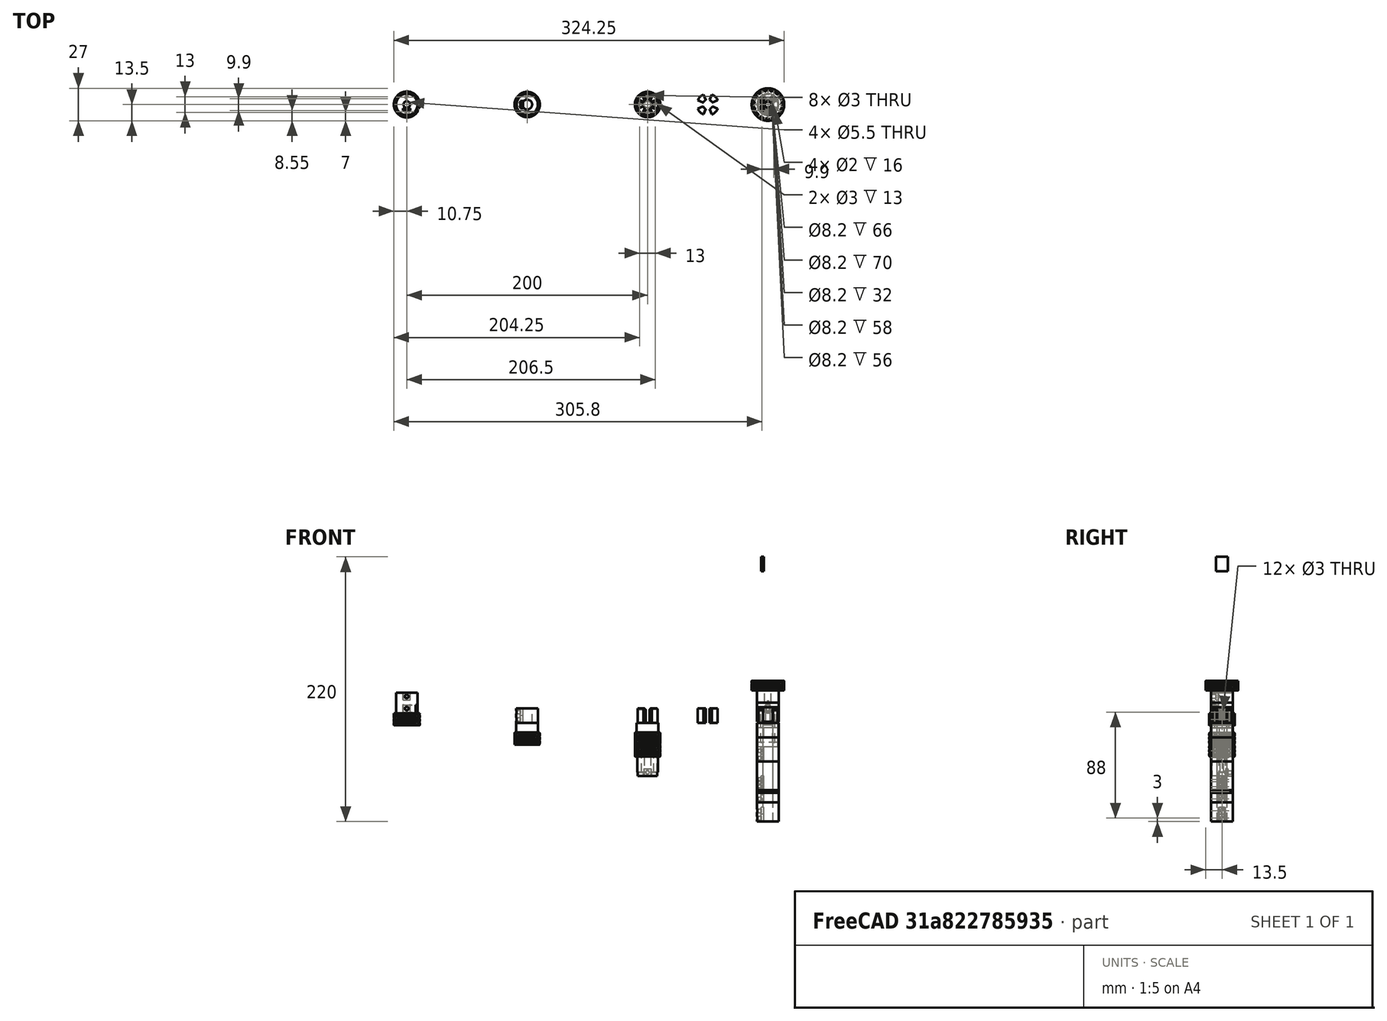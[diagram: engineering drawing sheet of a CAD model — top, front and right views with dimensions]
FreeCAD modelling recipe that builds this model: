
FCSTD DOCUMENT  (FreeCAD 0.19R24276 (Git))
Label: J-max_moto-shaft_009
License: All rights reserved
LicenseURL: http://en.wikipedia.org/wiki/All_rights_reserved
objects: Part::Cylinder×62, Part::Compound×46, Part::Chamfer×44, Part::Cut×37, Part::Wedge×36, Part::FeaturePython×28, Part::Box×18, Part::MultiFuse×3, Mesh::Feature×1
note: 274 computed .brp shape members not serialized (recipe doc carries the construction recipe); baked Part::Feature solids carry a one-line shape summary decoded from their .brp

FEATURE [Part::Cylinder] Cylinder032  label="Válec032"
  Angle = 360
  AttacherType = Attacher::AttachEngine3D
  Height = 3
  Placement = pos=(0,-6,0) rot=(0,0,1;0rad)
  Radius = 3
FEATURE [Part::Cylinder] Cylinder031  label="Válec031"
  Angle = 360
  AttacherType = Attacher::AttachEngine3D
  Height = 17
  Placement = pos=(0,6,3) rot=(0,0,1;0rad)
  Radius = 1.5
FEATURE [Part::Cylinder] Cylinder033  label="Válec033"
  Angle = 360
  AttacherType = Attacher::AttachEngine3D
  Height = 3
  Placement = pos=(0,6,0) rot=(0,0,1;0rad)
  Radius = 3
FEATURE [Part::Cylinder] Cylinder037  label="Válec037"
  Angle = 360
  AttacherType = Attacher::AttachEngine3D
  Height = 100
  Placement = pos=(100,-1,24) rot=(1,0,0;1.5708rad)
  Radius = 1.5
FEATURE [Part::FeaturePython] wormgear006  # WARN: FeaturePython — macro-defined, semantics opaque (R4)
  AttacherType = Attacher::AttachEngine3D
  Placement = pos=(0,0,0) rot=(0,0,1;0.663225rad)
  beta = 31.6075
  clearance = 0.2
  diameter = 19.5
  head = 0
  height = 10
  module = 1
  pressure_angle = 25
  reverse_pitch = true
  teeth = 12
  version = 0.0.3
FEATURE [Part::FeaturePython] wormgear004  # WARN: FeaturePython — macro-defined, semantics opaque (R4)
  AttacherType = Attacher::AttachEngine3D
  Placement = pos=(0,0,10) rot=(0,0,1;0.558505rad)
  beta = 31.6075
  clearance = 0.2
  diameter = 19.5
  head = 0
  height = 10
  module = 1
  pressure_angle = 25
  reverse_pitch = false
  teeth = 12
  version = 0.0.3
FEATURE [Part::Compound] Compound
  Links = -> [wormgear006,wormgear004]
FEATURE [Part::FeaturePython] Compound_child1  label="Compound.1"  # WARN: FeaturePython — macro-defined, semantics opaque (R4)
  Base = -> Compound
  FilterType = 1
  Invert = false
  OverrideMaxVal = 0
  WindowFrom = 80
  WindowTo = 100
  items = 1
FEATURE [Part::FeaturePython] Tube  # WARN: FeaturePython — macro-defined, semantics opaque (R4)
  AttacherType = Attacher::AttachEngine3D
  Height = 17
  InnerRadius = 2.75
  OuterRadius = 9
  Placement = pos=(0,0,20) rot=(0,0,1;0rad)
FEATURE [Part::Cylinder] Cylinder  label="Válec"
  Angle = 360
  AttacherType = Attacher::AttachEngine3D
  Height = 100
  Placement = pos=(100,-1,34) rot=(1,0,0;1.5708rad)
  Radius = 1.5
FEATURE [Part::Cylinder] Cylinder036  label="Válec036"
  Angle = 360
  AttacherType = Attacher::AttachEngine3D
  Height = 17
  Placement = pos=(0,-6,3) rot=(0,0,1;0rad)
  Radius = 1.5
FEATURE [Part::Compound] Compound006
  Links = -> [Cylinder036,Cylinder032,Cylinder033,Cylinder031]
FEATURE [Part::Box] Box  label="Krychle"
  AttacherType = Attacher::AttachEngine3D
  Height = 6
  Length = 6
  Placement = pos=(97,-5,31) rot=(0,0,1;0rad)
  Width = 2
FEATURE [Part::Cylinder] Cylinder019  label="Válec019"
  Angle = 360
  AttacherType = Attacher::AttachEngine3D
  Height = 60
  Placement = pos=(0,0,-10) rot=(0,0,1;0rad)
  Radius = 2.75
FEATURE [Part::Cut] Cut003
  Base = -> Compound_child1
  Tool = -> Cylinder019
FEATURE [Part::Compound] Compound016
  Links = -> [Cut003,Tube]
FEATURE [Part::Cut] Cut014  label="inner_p2"
  Base = -> Compound016
  Placement = pos=(100,0,0) rot=(0,0,1;0rad)
  Tool = -> Compound006
FEATURE [Part::Cut] Cut
  Base = -> Cut014
  Tool = -> Cylinder
FEATURE [Part::Cut] Cut015
  Base = -> Cut
  Tool = -> Box
FEATURE [Part::Box] Box001  label="Krychle001"
  AttacherType = Attacher::AttachEngine3D
  Height = 6
  Length = 14
  Placement = pos=(97,-5,21) rot=(0,0,1;0rad)
  Width = 2
FEATURE [Part::Cut] Cut016
  Base = -> Cut015
  Tool = -> Box001
FEATURE [Part::Cut] Cut017  label="planeo_vnitrni_hladko"
  Base = -> Cut016
  Tool = -> Cylinder037
FEATURE [Part::FeaturePython] Tube001  # WARN: FeaturePython — macro-defined, semantics opaque (R4)
  AttacherType = Attacher::AttachEngine3D
  Height = 12
  InnerRadius = 4.1
  OuterRadius = 9
  Placement = pos=(200,0,12) rot=(0,0,1;0rad)
FEATURE [Part::Box] Box002  label="Krychle002"
  AttacherType = Attacher::AttachEngine3D
  Height = 12
  Length = 2
  Placement = pos=(194.5,-5,12) rot=(0,0,1;0rad)
  Width = 10
FEATURE [Part::Cylinder] Cylinder039  label="Válec039"
  Angle = 360
  AttacherType = Attacher::AttachEngine3D
  Height = 100
  Placement = pos=(100,0,21) rot=(0.57735,0.57735,0.57735;2.0944rad)
  Radius = 1.5
FEATURE [Part::Box] Box003  label="Krychle003"
  AttacherType = Attacher::AttachEngine3D
  Height = 6
  Length = 6
  Placement = pos=(196.5,-3,18) rot=(0,0,1;1.5708rad)
  Width = 2
FEATURE [Part::MultiFuse] Fusion
  Shapes = -> [Tube001,Box002]
FEATURE [Part::Box] Box004  label="Krychle004"
  AttacherType = Attacher::AttachEngine3D
  Height = 6
  Length = 6
  Placement = pos=(196.5,-3,12) rot=(0,0,1;1.5708rad)
  Width = 2
FEATURE [Part::Cylinder] Cylinder040  label="Válec040"
  Angle = 360
  AttacherType = Attacher::AttachEngine3D
  Height = 100
  Placement = pos=(100,0,15) rot=(0.57735,0.57735,0.57735;2.0944rad)
  Radius = 1.5
FEATURE [Part::Compound] Compound017
  Links = -> [Box003,Box004]
FEATURE [Part::Cut] Cut018
  Base = -> Fusion
  Tool = -> Compound017
FEATURE [Part::Cylinder] Cylinder041  label="Válec041"
  Angle = 360
  AttacherType = Attacher::AttachEngine3D
  Height = 8
  Placement = pos=(200,0,4) rot=(0,0,1;0rad)
  Radius = 9
FEATURE [Part::Cylinder] Cylinder042  label="Válec042"
  Angle = 360
  AttacherType = Attacher::AttachEngine3D
  Height = 3
  Placement = pos=(0,-6.5,0) rot=(0,0,1;0rad)
  Radius = 3
FEATURE [Part::Cylinder] Cylinder043  label="Válec043"
  Angle = 360
  AttacherType = Attacher::AttachEngine3D
  Height = 3
  Placement = pos=(0,6.5,0) rot=(0,0,1;0rad)
  Radius = 3
FEATURE [Part::Cylinder] Cylinder044  label="Válec044"
  Angle = 360
  AttacherType = Attacher::AttachEngine3D
  Height = 26
  Placement = pos=(0,-6.5,3) rot=(0,0,1;0rad)
  Radius = 1.5
FEATURE [Part::Cylinder] Cylinder045  label="Válec045"
  Angle = 360
  AttacherType = Attacher::AttachEngine3D
  Height = 26
  Placement = pos=(0,6.5,3) rot=(0,0,1;0rad)
  Radius = 1.5
FEATURE [Part::Compound] Compound019
  Links = -> [Cylinder044,Cylinder042,Cylinder043,Cylinder045]
  Placement = pos=(200,0,-25) rot=(0,0,1;0rad)
FEATURE [Part::FeaturePython] wormgear007  # WARN: FeaturePython — macro-defined, semantics opaque (R4)
  AttacherType = Attacher::AttachEngine3D
  Placement = pos=(200,0,-6) rot=(0,0,1;0.558505rad)
  beta = 32.2756
  clearance = 0.2
  diameter = 19
  head = 0
  height = 10
  module = 1
  pressure_angle = 25
  reverse_pitch = true
  teeth = 12
  version = 0.0.3
FEATURE [Part::Cut] Cut020
  Base = -> wormgear007
  Tool = -> Compound019
FEATURE [Part::Compound] Compound018
  Links = -> [Cylinder039,Cylinder040]
FEATURE [Part::Cut] Cut019  label="super_spojka"
  Base = -> Cut018
  Tool = -> Compound018
FEATURE [Part::Compound] Compound020  label="super_spojka_s_vnitrnim_koleckem"
  Links = -> [Cylinder041,Cut020,Cut019]
FEATURE [Part::FeaturePython] Tube002  # WARN: FeaturePython — macro-defined, semantics opaque (R4)
  AttacherType = Attacher::AttachEngine3D
  Height = 12
  InnerRadius = 4.1
  OuterRadius = 9
  Placement = pos=(300,0,12) rot=(0,0,1;0rad)
FEATURE [Part::Cylinder] Cylinder046  label="Válec046"
  Angle = 360
  AttacherType = Attacher::AttachEngine3D
  Height = 8
  Placement = pos=(300,0,4) rot=(0,0,1;0rad)
  Radius = 9
FEATURE [Part::Cylinder] Cylinder047  label="Válec047"
  Angle = 360
  AttacherType = Attacher::AttachEngine3D
  Height = 26
  Placement = pos=(0,6.5,3) rot=(0,0,1;0rad)
  Radius = 1.5
FEATURE [Part::FeaturePython] wormgear008  # WARN: FeaturePython — macro-defined, semantics opaque (R4)
  AttacherType = Attacher::AttachEngine3D
  Placement = pos=(200,0,-6) rot=(0,0,1;0.558505rad)
  beta = 32.14
  clearance = 0.2
  diameter = 19.1
  head = 0
  height = 10
  module = 1
  pressure_angle = 25
  reverse_pitch = true
  teeth = 12
  version = 0.0.3
FEATURE [Part::Cylinder] Cylinder048  label="Válec048"
  Angle = 360
  AttacherType = Attacher::AttachEngine3D
  Height = 26
  Placement = pos=(0,-6.5,3) rot=(0,0,1;0rad)
  Radius = 1.5
FEATURE [Part::Cylinder] Cylinder049  label="Válec049"
  Angle = 360
  AttacherType = Attacher::AttachEngine3D
  Height = 3
  Placement = pos=(0,-6.5,0) rot=(0,0,1;0rad)
  Radius = 3
FEATURE [Part::Cylinder] Cylinder050  label="Válec050"
  Angle = 360
  AttacherType = Attacher::AttachEngine3D
  Height = 3
  Placement = pos=(0,6.5,0) rot=(0,0,1;0rad)
  Radius = 3
FEATURE [Part::Compound] Compound021
  Links = -> [Cylinder048,Cylinder049,Cylinder050,Cylinder047]
  Placement = pos=(200,0,-25) rot=(0,0,1;0rad)
FEATURE [Part::Cut] Cut021
  Base = -> wormgear008
  Placement = pos=(100,0,0) rot=(0,0,1;0rad)
  Tool = -> Compound021
FEATURE [Part::Wedge] Wedge  label="Klín"
  AttacherType = Attacher::AttachEngine3D
  Placement = pos=(300,0,12) rot=(0,0,1;0rad)
  X2max = 0
  X2min = 0
  Xmax = 10
  Xmin = -10
  Ymax = 0
  Ymin = -24.14
  Z2max = 12
  Z2min = 0
  Zmax = 12
  Zmin = 0
FEATURE [Part::Wedge] Wedge001  label="Klín001"
  AttacherType = Attacher::AttachEngine3D
  Placement = pos=(300,0,12) rot=(0,0,1;1.5708rad)
  X2max = 0
  X2min = 0
  Xmax = 10
  Xmin = -10
  Ymax = 0
  Ymin = -24.14
  Z2max = 12
  Z2min = 0
  Zmax = 12
  Zmin = 0
FEATURE [Part::Wedge] Wedge002  label="Klín002"
  AttacherType = Attacher::AttachEngine3D
  Placement = pos=(300,0,12) rot=(0,0,1;3.14159rad)
  X2max = 0
  X2min = 0
  Xmax = 10
  Xmin = -10
  Ymax = 0
  Ymin = -24.14
  Z2max = 12
  Z2min = 0
  Zmax = 12
  Zmin = 0
FEATURE [Part::Wedge] Wedge003  label="Klín003"
  AttacherType = Attacher::AttachEngine3D
  Placement = pos=(300,0,12) rot=(0,0,-1;1.5708rad)
  X2max = 0
  X2min = 0
  Xmax = 10
  Xmin = -10
  Ymax = 0
  Ymin = -24.14
  Z2max = 12
  Z2min = 0
  Zmax = 12
  Zmin = 0
FEATURE [Part::Compound] Compound022
  Links = -> [Wedge,Wedge001,Wedge002,Wedge003]
FEATURE [Part::Cut] Cut022
  Base = -> Tube002
  Tool = -> Compound022
FEATURE [Part::FeaturePython] Tube003  # WARN: FeaturePython — macro-defined, semantics opaque (R4)
  AttacherType = Attacher::AttachEngine3D
  Height = 12
  InnerRadius = 4.1
  OuterRadius = 9
  Placement = pos=(300,0,12) rot=(0,0,1;0rad)
FEATURE [Part::Wedge] Wedge004  label="Klín004"
  AttacherType = Attacher::AttachEngine3D
  Placement = pos=(300,0,12) rot=(0,0,1;1.5708rad)
  X2max = 0
  X2min = 0
  Xmax = 10
  Xmin = -10
  Ymax = 0
  Ymin = -24.14
  Z2max = 12
  Z2min = 0
  Zmax = 12
  Zmin = 0
FEATURE [Part::Wedge] Wedge005  label="Klín005"
  AttacherType = Attacher::AttachEngine3D
  Placement = pos=(300,0,12) rot=(0,0,1;3.14159rad)
  X2max = 0
  X2min = 0
  Xmax = 10
  Xmin = -10
  Ymax = 0
  Ymin = -24.14
  Z2max = 12
  Z2min = 0
  Zmax = 12
  Zmin = 0
FEATURE [Part::Wedge] Wedge006  label="Klín006"
  AttacherType = Attacher::AttachEngine3D
  Placement = pos=(300,0,12) rot=(0,0,-1;1.5708rad)
  X2max = 0
  X2min = 0
  Xmax = 10
  Xmin = -10
  Ymax = 0
  Ymin = -24.14
  Z2max = 12
  Z2min = 0
  Zmax = 12
  Zmin = 0
FEATURE [Part::Wedge] Wedge007  label="Klín007"
  AttacherType = Attacher::AttachEngine3D
  Placement = pos=(300,0,12) rot=(0,0,1;0rad)
  X2max = 0
  X2min = 0
  Xmax = 10
  Xmin = -10
  Ymax = 0
  Ymin = -24.14
  Z2max = 12
  Z2min = 0
  Zmax = 12
  Zmin = 0
FEATURE [Part::Compound] Compound023
  Links = -> [Wedge007,Wedge004,Wedge005,Wedge006]
FEATURE [Part::Cut] Cut023
  Base = -> Tube003
  Placement = pos=(50,0,0) rot=(0,0,1;0rad)
  Tool = -> Compound023
FEATURE [Part::Compound] Compound024
  Links = -> [Cylinder046,Cut021,Cut022]
FEATURE [Part::Chamfer] Chamfer
  Base = -> Compound024
  Edges = 1 edges r=1: [Edge196]
FEATURE [Part::Chamfer] Chamfer001
  Base = -> Chamfer
  Edges = 1 edges r=1: [Edge187]
FEATURE [Part::Chamfer] Chamfer002
  Base = -> Chamfer001
  Edges = 1 edges r=1: [Edge7]
FEATURE [Part::Chamfer] Chamfer003
  Base = -> Chamfer002
  Edges = 1 edges r=1: [Edge196]
FEATURE [Part::Chamfer] Chamfer004
  Base = -> Chamfer003
  Edges = 1 edges r=1: [Edge206]
FEATURE [Part::Chamfer] Chamfer005
  Base = -> Chamfer004
  Edges = 1 edges r=1: [Edge28]
FEATURE [Part::Chamfer] Chamfer006  label="spojka_aktuarni"
  Base = -> Chamfer005
  Edges = 1 edges r=1: [Edge58]
FEATURE [Part::Wedge] Wedge008  label="Klín008"
  AttacherType = Attacher::AttachEngine3D
  Placement = pos=(400,0,12) rot=(0,0,1;0rad)
  X2max = 0
  X2min = 0
  Xmax = 10
  Xmin = -10
  Ymax = 0
  Ymin = -20
  Z2max = 12
  Z2min = 0
  Zmax = 12
  Zmin = 0
FEATURE [Part::Wedge] Wedge009  label="Klín009"
  AttacherType = Attacher::AttachEngine3D
  Placement = pos=(400,0,12) rot=(0,0,1;1.5708rad)
  X2max = 0
  X2min = 0
  Xmax = 10
  Xmin = -10
  Ymax = 0
  Ymin = -20
  Z2max = 12
  Z2min = 0
  Zmax = 12
  Zmin = 0
FEATURE [Part::Wedge] Wedge010  label="Klín010"
  AttacherType = Attacher::AttachEngine3D
  Placement = pos=(400,0,12) rot=(0,0,1;3.14159rad)
  X2max = 0
  X2min = 0
  Xmax = 10
  Xmin = -10
  Ymax = 0
  Ymin = -20
  Z2max = 12
  Z2min = 0
  Zmax = 12
  Zmin = 0
FEATURE [Part::Wedge] Wedge011  label="Klín011"
  AttacherType = Attacher::AttachEngine3D
  Placement = pos=(400,0,12) rot=(0,0,-1;1.5708rad)
  X2max = 0
  X2min = 0
  Xmax = 10
  Xmin = -10
  Ymax = 0
  Ymin = -20
  Z2max = 12
  Z2min = 0
  Zmax = 12
  Zmin = 0
FEATURE [Part::FeaturePython] Tube004  # WARN: FeaturePython — macro-defined, semantics opaque (R4)
  AttacherType = Attacher::AttachEngine3D
  Height = 12
  InnerRadius = 4.1
  OuterRadius = 9
  Placement = pos=(400,0,12) rot=(0,0,1;0rad)
FEATURE [Part::Box] Box005  label="Krychle005"
  AttacherType = Attacher::AttachEngine3D
  Height = 6
  Length = 6
  Placement = pos=(196.5,-3,12) rot=(0,0,1;1.5708rad)
  Width = 2
FEATURE [Part::Cylinder] Cylinder051  label="Válec051"
  Angle = 360
  AttacherType = Attacher::AttachEngine3D
  Height = 100
  Placement = pos=(100,0,15) rot=(0.57735,0.57735,0.57735;2.0944rad)
  Radius = 1.5
FEATURE [Part::Box] Box006  label="Krychle006"
  AttacherType = Attacher::AttachEngine3D
  Height = 12
  Length = 2
  Placement = pos=(194.5,-5,12) rot=(0,0,1;0rad)
  Width = 10
FEATURE [Part::Box] Box007  label="Krychle007"
  AttacherType = Attacher::AttachEngine3D
  Height = 6
  Length = 6
  Placement = pos=(196.5,-3,18) rot=(0,0,1;1.5708rad)
  Width = 2
FEATURE [Part::Compound] Compound025
  Links = -> [Box007,Box005]
  Placement = pos=(0,0,-20) rot=(0,0,1;0rad)
FEATURE [Part::Cylinder] Cylinder052  label="Válec052"
  Angle = 360
  AttacherType = Attacher::AttachEngine3D
  Height = 100
  Placement = pos=(100,0,21) rot=(0.57735,0.57735,0.57735;2.0944rad)
  Radius = 1.5
FEATURE [Part::Compound] Compound026
  Links = -> [Cylinder052,Cylinder051]
  Placement = pos=(0,0,-20) rot=(0,0,1;0rad)
FEATURE [Part::FeaturePython] Tube005  # WARN: FeaturePython — macro-defined, semantics opaque (R4)
  AttacherType = Attacher::AttachEngine3D
  Height = 32
  InnerRadius = 4.1
  OuterRadius = 9
  Placement = pos=(200,0,-8) rot=(0,0,1;0rad)
FEATURE [Part::MultiFuse] Fusion001
  Shapes = -> [Tube005,Box006]
FEATURE [Part::Cut] Cut024
  Base = -> Fusion001
  Tool = -> Compound025
FEATURE [Part::Cut] Cut025  label="super_spojka001"
  Base = -> Cut024
  Placement = pos=(200,0,-12) rot=(0,0,1;0rad)
  Tool = -> Compound026
FEATURE [Part::Compound] Compound027
  Links = -> [Wedge011,Wedge008,Wedge009,Wedge010]
FEATURE [Part::Cut] Cut026
  Base = -> Tube004
  Tool = -> Compound027
FEATURE [Part::Compound] Compound028  label="spojka"
  Links = -> [Cut026,Cut025]
FEATURE [Part::Cylinder] Cylinder053  label="Válec053"
  Angle = 360
  AttacherType = Attacher::AttachEngine3D
  Height = 12
  Placement = pos=(400,0,10) rot=(0,0,1;0rad)
  Radius = 4
FEATURE [Part::Chamfer] Chamfer007
  Base = -> Cylinder053
  Edges = 1 edges r=1: [Edge1]
FEATURE [Part::Chamfer] Chamfer008
  Base = -> Compound028
  Edges = 1 edges r=1: [Edge41]
FEATURE [Part::Chamfer] Chamfer009
  Base = -> Chamfer008
  Edges = 1 edges r=1: [Edge8]
FEATURE [Part::Chamfer] Chamfer010
  Base = -> Chamfer009
  Edges = 1 edges r=1: [Edge52]
FEATURE [Part::Chamfer] Chamfer011
  Base = -> Chamfer010
  Edges = 1 edges r=1: [Edge13]
FEATURE [Part::Chamfer] Chamfer012
  Base = -> Chamfer011
  Edges = 1 edges r=1: [Edge41]
FEATURE [Part::Chamfer] Chamfer013
  Base = -> Chamfer012
  Edges = 1 edges r=1: [Edge56]
FEATURE [Part::Chamfer] Chamfer014
  Base = -> Chamfer013
  Edges = 1 edges r=1: [Edge8]
FEATURE [Part::Chamfer] Chamfer015
  Base = -> Chamfer014
  Edges = 1 edges r=1: [Edge32]
FEATURE [Part::Compound] Compound029  label="spojka_motorova"
  Links = -> [Chamfer015,Chamfer007]
FEATURE [Part::Cylinder] Cylinder054  label="Válec054"
  Angle = 360
  AttacherType = Attacher::AttachEngine3D
  Height = 3
  Placement = pos=(0,-6.5,0) rot=(0,0,1;0rad)
  Radius = 3
FEATURE [Part::Cylinder] Cylinder055  label="Válec055"
  Angle = 360
  AttacherType = Attacher::AttachEngine3D
  Height = 50
  Placement = pos=(0,6.5,3) rot=(0,0,1;0rad)
  Radius = 1.5
FEATURE [Part::Cylinder] Cylinder056  label="Válec056"
  Angle = 360
  AttacherType = Attacher::AttachEngine3D
  Height = 3
  Placement = pos=(0,6.5,0) rot=(0,0,1;0rad)
  Radius = 3
FEATURE [Part::FeaturePython] wormgear009  # WARN: FeaturePython — macro-defined, semantics opaque (R4)
  AttacherType = Attacher::AttachEngine3D
  Placement = pos=(0,0,10) rot=(0,0,1;0.383972rad)
  beta = 32.14
  clearance = 0.2
  diameter = 19.1
  head = 0
  height = 10
  module = 1
  pressure_angle = 25
  reverse_pitch = false
  teeth = 12
  version = 0.0.3
FEATURE [Part::FeaturePython] wormgear010  # WARN: FeaturePython — macro-defined, semantics opaque (R4)
  AttacherType = Attacher::AttachEngine3D
  Placement = pos=(0,0,0) rot=(0,0,1;0.645772rad)
  beta = 30.9638
  clearance = 0.2
  diameter = 20
  head = 0
  height = 10
  module = 1
  pressure_angle = 25
  reverse_pitch = true
  teeth = 12
  version = 0.0.3
FEATURE [Part::Compound] Compound031
  Links = -> [wormgear010,wormgear009]
FEATURE [Part::FeaturePython] Compound_child002  label="Compound.002"  # WARN: FeaturePython — macro-defined, semantics opaque (R4)
  Base = -> Compound031
  FilterType = 1
  Invert = false
  OverrideMaxVal = 0
  WindowFrom = 80
  WindowTo = 100
  items = 1
FEATURE [Part::FeaturePython] Tube006  # WARN: FeaturePython — macro-defined, semantics opaque (R4)
  AttacherType = Attacher::AttachEngine3D
  Height = 16
  InnerRadius = 2.75
  OuterRadius = 8.5
  Placement = pos=(0,0,20) rot=(0,0,1;0rad)
FEATURE [Part::Box] Box008  label="Krychle008"
  AttacherType = Attacher::AttachEngine3D
  Height = 6
  Length = 6
  Placement = pos=(97,-5,30) rot=(0,0,1;0rad)
  Width = 2
FEATURE [Part::Cylinder] Cylinder057  label="Válec057"
  Angle = 360
  AttacherType = Attacher::AttachEngine3D
  Height = 50
  Placement = pos=(0,-6.5,3) rot=(0,0,1;0rad)
  Radius = 1.5
FEATURE [Part::Cylinder] Cylinder058  label="Válec058"
  Angle = 360
  AttacherType = Attacher::AttachEngine3D
  Height = 100
  Placement = pos=(100,-1,33) rot=(1,0,0;1.5708rad)
  Radius = 1.5
FEATURE [Part::Cylinder] Cylinder059  label="Válec059"
  Angle = 360
  AttacherType = Attacher::AttachEngine3D
  Height = 50
  Placement = pos=(0,0,-10) rot=(0,0,1;0rad)
  Radius = 2.75
FEATURE [Part::Cut] Cut027
  Base = -> Compound_child002
  Tool = -> Cylinder059
FEATURE [Part::Compound] Compound030
  Links = -> [Cut027,Tube006]
FEATURE [Part::Compound] Compound032
  Links = -> [Cylinder057,Cylinder054,Cylinder056,Cylinder055]
  Placement = pos=(0,0,36) rot=(0.707107,0.707107,0;3.14159rad)
FEATURE [Part::Cut] Cut029  label="inner_p003"
  Base = -> Compound030
  Placement = pos=(100,0,0) rot=(0,0,1;0rad)
  Tool = -> Compound032
FEATURE [Part::Cut] Cut028
  Base = -> Cut029
  Tool = -> Cylinder058
FEATURE [Part::Cut] Cut030  label="planeo_vnitrni_sroubene"
  Base = -> Cut028
  Placement = pos=(200,0,4) rot=(1,0,0;3.14159rad)
  Tool = -> Box008
FEATURE [Part::Wedge] Wedge012  label="Klín012"
  AttacherType = Attacher::AttachEngine3D
  Placement = pos=(400,0,12) rot=(0,0,1;0rad)
  X2max = 0
  X2min = 0
  Xmax = 10
  Xmin = -10
  Ymax = 0
  Ymin = -20
  Z2max = 12
  Z2min = 0
  Zmax = 12
  Zmin = 0
FEATURE [Part::Wedge] Wedge013  label="Klín013"
  AttacherType = Attacher::AttachEngine3D
  Placement = pos=(400,0,12) rot=(0,0,1;1.5708rad)
  X2max = 0
  X2min = 0
  Xmax = 10
  Xmin = -10
  Ymax = 0
  Ymin = -20
  Z2max = 12
  Z2min = 0
  Zmax = 12
  Zmin = 0
FEATURE [Part::Wedge] Wedge014  label="Klín014"
  AttacherType = Attacher::AttachEngine3D
  Placement = pos=(400,0,12) rot=(0,0,1;3.14159rad)
  X2max = 0
  X2min = 0
  Xmax = 10
  Xmin = -10
  Ymax = 0
  Ymin = -20
  Z2max = 12
  Z2min = 0
  Zmax = 12
  Zmin = 0
FEATURE [Part::Wedge] Wedge015  label="Klín015"
  AttacherType = Attacher::AttachEngine3D
  Placement = pos=(400,0,12) rot=(0,0,-1;1.5708rad)
  X2max = 0
  X2min = 0
  Xmax = 10
  Xmin = -10
  Ymax = 0
  Ymin = -20
  Z2max = 12
  Z2min = 0
  Zmax = 12
  Zmin = 0
FEATURE [Part::Compound] Compound033
  Links = -> [Wedge015,Wedge012,Wedge013,Wedge014]
FEATURE [Part::FeaturePython] Tube007  # WARN: FeaturePython — macro-defined, semantics opaque (R4)
  AttacherType = Attacher::AttachEngine3D
  Height = 12
  InnerRadius = 4.1
  OuterRadius = 8.25
  Placement = pos=(400,0,12) rot=(0,0,1;0rad)
FEATURE [Part::Cut] Cut033
  Base = -> Tube007
  Tool = -> Compound033
FEATURE [Part::Compound] Compound035  label="spojka001"
  Links = -> [Cut033]
FEATURE [Part::Cylinder] Cylinder062  label="Válec062"
  Angle = 360
  AttacherType = Attacher::AttachEngine3D
  Height = 12
  Placement = pos=(400,0,10) rot=(0,0,1;0rad)
  Radius = 4
FEATURE [Part::Chamfer] Chamfer021
  Base = -> Cylinder062
  Edges = 1 edges r=1: [Edge1]
FEATURE [Part::Chamfer] Chamfer022
  Base = -> Compound035
  Edges = 1 edges r=1: [Edge41]
FEATURE [Part::Chamfer] Chamfer023
  Base = -> Chamfer022
  Edges = 1 edges r=1: [Edge8]
FEATURE [Part::Chamfer] Chamfer024
  Base = -> Chamfer023
  Edges = 1 edges r=1: [Edge52]
FEATURE [Part::Chamfer] Chamfer018
  Base = -> Chamfer024
  Edges = 1 edges r=1: [Edge13]
FEATURE [Part::Chamfer] Chamfer016
  Base = -> Chamfer018
  Edges = 1 edges r=1: [Edge41]
FEATURE [Part::Chamfer] Chamfer017
  Base = -> Chamfer016
  Edges = 1 edges r=1: [Edge56]
FEATURE [Part::Chamfer] Chamfer020
  Base = -> Chamfer017
  Edges = 1 edges r=1: [Edge8]
FEATURE [Part::Chamfer] Chamfer019
  Base = -> Chamfer020
  Edges = 1 edges r=1: [Edge32]
FEATURE [Part::Compound] Compound034  label="spojka_motorova_bocni"
  Links = -> [Chamfer019,Chamfer021]
FEATURE [Part::FeaturePython] Tube009  # WARN: FeaturePython — macro-defined, semantics opaque (R4)
  AttacherType = Attacher::AttachEngine3D
  Height = 16
  InnerRadius = 4.1
  OuterRadius = 8.25
  Placement = pos=(400,0,-8) rot=(0,0,1;0rad)
FEATURE [Part::Cylinder] Cylinder063  label="Válec063"
  Angle = 360
  AttacherType = Attacher::AttachEngine3D
  Height = 16
  Placement = pos=(400,0,-4) rot=(0,0,1;0rad)
  Radius = 8.25
FEATURE [Part::Compound] Compound036  label="motorova_spojka_bocni"
  Links = -> [Cylinder063,Compound034]
FEATURE [Part::FeaturePython] Tube010  # WARN: FeaturePython — macro-defined, semantics opaque (R4)
  AttacherType = Attacher::AttachEngine3D
  Height = 12
  InnerRadius = 4.1
  OuterRadius = 9
  Placement = pos=(400,0,12) rot=(0,0,1;0rad)
FEATURE [Part::Cylinder] Cylinder064  label="Válec064"
  Angle = 360
  AttacherType = Attacher::AttachEngine3D
  Height = 100
  Placement = pos=(100,0,15) rot=(0.57735,0.57735,0.57735;2.0944rad)
  Radius = 1.5
FEATURE [Part::Cylinder] Cylinder065  label="Válec065"
  Angle = 360
  AttacherType = Attacher::AttachEngine3D
  Height = 100
  Placement = pos=(100,0,21) rot=(0.57735,0.57735,0.57735;2.0944rad)
  Radius = 1.5
FEATURE [Part::Compound] Compound038
  Links = -> [Cylinder065,Cylinder064]
  Placement = pos=(0,0,-20) rot=(0,0,1;0rad)
FEATURE [Part::Cylinder] Cylinder066  label="Válec066"
  Angle = 360
  AttacherType = Attacher::AttachEngine3D
  Height = 12
  Placement = pos=(400,0,10) rot=(0,0,1;0rad)
  Radius = 4
FEATURE [Part::Box] Box009  label="Krychle009"
  AttacherType = Attacher::AttachEngine3D
  Height = 6
  Length = 6
  Placement = pos=(196.5,-3,12) rot=(0,0,1;1.5708rad)
  Width = 2
FEATURE [Part::Box] Box010  label="Krychle010"
  AttacherType = Attacher::AttachEngine3D
  Height = 6
  Length = 6
  Placement = pos=(196.5,-3,18) rot=(0,0,1;1.5708rad)
  Width = 2
FEATURE [Part::Compound] Compound041
  Links = -> [Box010,Box009]
  Placement = pos=(0,0,-20) rot=(0,0,1;0rad)
FEATURE [Part::Wedge] Wedge016  label="Klín016"
  AttacherType = Attacher::AttachEngine3D
  Placement = pos=(400,0,12) rot=(0,0,1;0rad)
  X2max = 0
  X2min = 0
  Xmax = 10
  Xmin = -10
  Ymax = 0
  Ymin = -19
  Z2max = 12
  Z2min = 0
  Zmax = 12
  Zmin = 0
FEATURE [Part::Wedge] Wedge017  label="Klín017"
  AttacherType = Attacher::AttachEngine3D
  Placement = pos=(400,0,12) rot=(0,0,1;1.5708rad)
  X2max = 0
  X2min = 0
  Xmax = 10
  Xmin = -10
  Ymax = 0
  Ymin = -19
  Z2max = 12
  Z2min = 0
  Zmax = 12
  Zmin = 0
FEATURE [Part::Wedge] Wedge018  label="Klín018"
  AttacherType = Attacher::AttachEngine3D
  Placement = pos=(400,0,12) rot=(0,0,1;3.14159rad)
  X2max = 0
  X2min = 0
  Xmax = 10
  Xmin = -10
  Ymax = 0
  Ymin = -19
  Z2max = 12
  Z2min = 0
  Zmax = 12
  Zmin = 0
FEATURE [Part::Wedge] Wedge019  label="Klín019"
  AttacherType = Attacher::AttachEngine3D
  Placement = pos=(400,0,12) rot=(0,0,-1;1.5708rad)
  X2max = 0
  X2min = 0
  Xmax = 10
  Xmin = -10
  Ymax = 0
  Ymin = -19
  Z2max = 12
  Z2min = 0
  Zmax = 12
  Zmin = 0
FEATURE [Part::Compound] Compound040
  Links = -> [Wedge019,Wedge016,Wedge017,Wedge018]
FEATURE [Part::Cut] Cut034
  Base = -> Tube010
  Tool = -> Compound040
FEATURE [Part::FeaturePython] Tube011  # WARN: FeaturePython — macro-defined, semantics opaque (R4)
  AttacherType = Attacher::AttachEngine3D
  Height = 70
  InnerRadius = 4.1
  OuterRadius = 9
  Placement = pos=(200,0,-8) rot=(0,0,1;0rad)
FEATURE [Part::Chamfer] Chamfer028
  Base = -> Cylinder066
  Edges = 1 edges r=1: [Edge1]
FEATURE [Part::Cylinder] Cylinder185  label="Válec185"
  Angle = 360
  AttacherType = Attacher::AttachEngine3D
  Height = 50
  Placement = pos=(0,0,-10) rot=(0,0,1;0rad)
  Radius = 2.65
FEATURE [Part::FeaturePython] wormgear030  # WARN: FeaturePython — macro-defined, semantics opaque (R4)
  AttacherType = Attacher::AttachEngine3D
  Placement = pos=(0,0,29) rot=(0,0,1;0.994838rad)
  beta = 30.9638
  clearance = 0.25
  diameter = 25
  head = 0
  height = 8
  module = 1
  pressure_angle = 20
  reverse_pitch = false
  teeth = 15
  version = 0.0.3
FEATURE [Part::Cut] Cut081
  Base = -> wormgear030
  Tool = -> Cylinder185
FEATURE [Part::FeaturePython] Tube018  # WARN: FeaturePython — macro-defined, semantics opaque (R4)
  AttacherType = Attacher::AttachEngine3D
  Height = 12
  InnerRadius = 4.1
  OuterRadius = 9
  Placement = pos=(0,0,12) rot=(0,0,1;0rad)
FEATURE [Part::Cylinder] Cylinder186  label="Válec186"
  Angle = 360
  AttacherType = Attacher::AttachEngine3D
  Height = 4
  Placement = pos=(0,0,15) rot=(0,0,1;0rad)
  Radius = 9
FEATURE [Part::Wedge] Wedge020  label="Klín020"
  AttacherType = Attacher::AttachEngine3D
  Placement = pos=(0,0,12) rot=(0,0,1;0rad)
  X2max = 0
  X2min = 0
  Xmax = 10
  Xmin = -10
  Ymax = 0
  Ymin = -32
  Z2max = 12
  Z2min = 0
  Zmax = 12
  Zmin = 0
FEATURE [Part::Wedge] Wedge021  label="Klín021"
  AttacherType = Attacher::AttachEngine3D
  Placement = pos=(0,0,12) rot=(0,0,1;1.5708rad)
  X2max = 0
  X2min = 0
  Xmax = 10
  Xmin = -10
  Ymax = 0
  Ymin = -32
  Z2max = 12
  Z2min = 0
  Zmax = 12
  Zmin = 0
FEATURE [Part::Wedge] Wedge022  label="Klín022"
  AttacherType = Attacher::AttachEngine3D
  Placement = pos=(0,0,12) rot=(0,0,1;3.14159rad)
  X2max = 0
  X2min = 0
  Xmax = 10
  Xmin = -10
  Ymax = 0
  Ymin = -32
  Z2max = 12
  Z2min = 0
  Zmax = 12
  Zmin = 0
FEATURE [Part::Wedge] Wedge023  label="Klín023"
  AttacherType = Attacher::AttachEngine3D
  Placement = pos=(0,0,12) rot=(0,0,-1;1.5708rad)
  X2max = 0
  X2min = 0
  Xmax = 10
  Xmin = -10
  Ymax = 0
  Ymin = -32
  Z2max = 12
  Z2min = 0
  Zmax = 12
  Zmin = 0
FEATURE [Part::Compound] Compound042
  Links = -> [Wedge020,Wedge021,Wedge022,Wedge023]
FEATURE [Part::Cut] Cut082
  Base = -> Tube018
  Placement = pos=(0,0,-9) rot=(0,0,1;0rad)
  Tool = -> Compound042
FEATURE [Part::Chamfer] Chamfer034
  Base = -> Cut082
  Edges = 8 edges r=1: [Edge7,Edge8,Edge21,Edge22,Edge31,Edge32,Edge45,Edge46]
FEATURE [Part::FeaturePython] Tube019  # WARN: FeaturePython — macro-defined, semantics opaque (R4)
  AttacherType = Attacher::AttachEngine3D
  Height = 10
  InnerRadius = 2.65
  OuterRadius = 9
  Placement = pos=(0,0,19) rot=(0,0,1;0rad)
FEATURE [Part::Compound] Compound210  label="J-max_inner-planeo"
  Links = -> [Chamfer034,Tube019,Cylinder186,Cut081]
  Placement = pos=(400,0,10) rot=(0,0,-1;0.785398rad)
FEATURE [Part::Box] Box011  label="Krychle011"
  AttacherType = Attacher::AttachEngine3D
  Height = 12
  Length = 2
  Placement = pos=(194.5,-5,200) rot=(0,0,1;0rad)
  Width = 10
FEATURE [Part::MultiFuse] Fusion002
  Shapes = -> [Tube011,Box011]
FEATURE [Part::Cut] Cut036
  Base = -> Fusion002
  Tool = -> Compound041
FEATURE [Part::Cut] Cut035  label="super_spojka002"
  Base = -> Cut036
  Placement = pos=(200,0,-62) rot=(0,0,1;0rad)
  Tool = -> Compound038
FEATURE [Part::Compound] Compound037  label="spojka002"
  Links = -> [Cut034,Cut035]
FEATURE [Part::Chamfer] Chamfer029
  Base = -> Compound037
  Edges = 1 edges r=1: [Edge41]
FEATURE [Part::Chamfer] Chamfer030
  Base = -> Chamfer029
  Edges = 1 edges r=1: [Edge8]
FEATURE [Part::Chamfer] Chamfer031
  Base = -> Chamfer030
  Edges = 1 edges r=1: [Edge52]
FEATURE [Part::Chamfer] Chamfer032
  Base = -> Chamfer031
  Edges = 1 edges r=1: [Edge13]
FEATURE [Part::Chamfer] Chamfer033
  Base = -> Chamfer032
  Edges = 1 edges r=1: [Edge41]
FEATURE [Part::Chamfer] Chamfer025
  Base = -> Chamfer033
  Edges = 1 edges r=1: [Edge56]
FEATURE [Part::Chamfer] Chamfer026
  Base = -> Chamfer025
  Edges = 1 edges r=1: [Edge8]
FEATURE [Part::Chamfer] Chamfer027
  Base = -> Chamfer026
  Edges = 1 edges r=1: [Edge32]
FEATURE [Part::Compound] Compound039  label="J-max_moto-clutch_old"
  Links = -> [Chamfer027,Chamfer028]
FEATURE [Part::Box] Box012  label="Krychle012"
  AttacherType = Attacher::AttachEngine3D
  Height = 6
  Length = 6
  Placement = pos=(196.5,-3,12) rot=(0,0,1;1.5708rad)
  Width = 2
FEATURE [Part::Box] Box013  label="Krychle013"
  AttacherType = Attacher::AttachEngine3D
  Height = 6
  Length = 6
  Placement = pos=(196.5,-3,18) rot=(0,0,1;1.5708rad)
  Width = 2
FEATURE [Part::Cylinder] Cylinder187  label="Válec187"
  Angle = 360
  AttacherType = Attacher::AttachEngine3D
  Height = 100
  Placement = pos=(100,0,15) rot=(0.57735,0.57735,0.57735;2.0944rad)
  Radius = 1.5
FEATURE [Part::Cylinder] Cylinder188  label="Válec188"
  Angle = 360
  AttacherType = Attacher::AttachEngine3D
  Height = 100
  Placement = pos=(100,0,21) rot=(0.57735,0.57735,0.57735;2.0944rad)
  Radius = 1.5
FEATURE [Part::Compound] Compound211
  Links = -> [Cylinder188,Cylinder187]
  Placement = pos=(0,0,-20) rot=(0,0,1;0rad)
FEATURE [Part::Compound] Compound212
  Links = -> [Box013,Box012]
  Placement = pos=(0,0,-20) rot=(0,0,1;0rad)
FEATURE [Part::FeaturePython] Tube020  # WARN: FeaturePython — macro-defined, semantics opaque (R4)
  AttacherType = Attacher::AttachEngine3D
  Height = 56
  InnerRadius = 4.1
  OuterRadius = 9
  Placement = pos=(200,0,-8) rot=(0,0,1;0rad)
FEATURE [Part::Cut] Cut083
  Base = -> Tube020
  Tool = -> Compound212
FEATURE [Part::Cut] Cut084
  Base = -> Cut083
  Placement = pos=(200,0,-36) rot=(0,0,1;0rad)
  Tool = -> Compound211
FEATURE [Part::Wedge] Wedge024  label="Klín024"
  AttacherType = Attacher::AttachEngine3D
  Placement = pos=(400,0,12) rot=(0,0,-1;1.5708rad)
  X2max = 0
  X2min = 0
  Xmax = 10
  Xmin = -10
  Ymax = 0
  Ymin = -19
  Z2max = 12
  Z2min = 0
  Zmax = 12
  Zmin = 0
FEATURE [Part::Wedge] Wedge025  label="Klín025"
  AttacherType = Attacher::AttachEngine3D
  Placement = pos=(400,0,12) rot=(0,0,1;3.14159rad)
  X2max = 0
  X2min = 0
  Xmax = 10
  Xmin = -10
  Ymax = 0
  Ymin = -19
  Z2max = 12
  Z2min = 0
  Zmax = 12
  Zmin = 0
FEATURE [Part::FeaturePython] Tube021  # WARN: FeaturePython — macro-defined, semantics opaque (R4)
  AttacherType = Attacher::AttachEngine3D
  Height = 12
  InnerRadius = 4.1
  OuterRadius = 9
  Placement = pos=(400,0,12) rot=(0,0,1;0rad)
FEATURE [Part::Cylinder] Cylinder189  label="Válec189"
  Angle = 360
  AttacherType = Attacher::AttachEngine3D
  Height = 12
  Placement = pos=(400,0,10) rot=(0,0,1;0rad)
  Radius = 4
FEATURE [Part::Chamfer] Chamfer035
  Base = -> Cylinder189
  Edges = 1 edges r=1: [Edge1]
FEATURE [Part::Wedge] Wedge026  label="Klín026"
  AttacherType = Attacher::AttachEngine3D
  Placement = pos=(400,0,12) rot=(0,0,1;0rad)
  X2max = 0
  X2min = 0
  Xmax = 10
  Xmin = -10
  Ymax = 0
  Ymin = -19
  Z2max = 12
  Z2min = 0
  Zmax = 12
  Zmin = 0
FEATURE [Part::Wedge] Wedge027  label="Klín027"
  AttacherType = Attacher::AttachEngine3D
  Placement = pos=(400,0,12) rot=(0,0,1;1.5708rad)
  X2max = 0
  X2min = 0
  Xmax = 10
  Xmin = -10
  Ymax = 0
  Ymin = -19
  Z2max = 12
  Z2min = 0
  Zmax = 12
  Zmin = 0
FEATURE [Part::Compound] Compound213
  Links = -> [Wedge024,Wedge026,Wedge027,Wedge025]
FEATURE [Part::Cut] Cut085
  Base = -> Tube021
  Tool = -> Compound213
FEATURE [Part::Chamfer] Chamfer036
  Base = -> Cut034
  Edges = 2 edges r=0.8: [Edge17,Edge19]
FEATURE [Part::Chamfer] Chamfer037
  Base = -> Chamfer036
  Edges = 6 edges r=0.8: [Edge23,Edge28,Edge35,Edge40,Edge47,Edge49]
FEATURE [Part::Compound] Compound214  label="J-max_motor-shaft"
  Links = -> [Cut084,Chamfer035,Chamfer037]
FEATURE [Part::Wedge] Wedge028  label="Klín028"
  AttacherType = Attacher::AttachEngine3D
  Placement = pos=(400,0,12) rot=(0,0,-1;1.5708rad)
  X2max = 0
  X2min = 0
  Xmax = 10
  Xmin = -10
  Ymax = 0
  Ymin = -19
  Z2max = 12
  Z2min = 0
  Zmax = 12
  Zmin = 0
FEATURE [Part::Wedge] Wedge029  label="Klín029"
  AttacherType = Attacher::AttachEngine3D
  Placement = pos=(400,0,12) rot=(0,0,1;3.14159rad)
  X2max = 0
  X2min = 0
  Xmax = 10
  Xmin = -10
  Ymax = 0
  Ymin = -19
  Z2max = 12
  Z2min = 0
  Zmax = 12
  Zmin = 0
FEATURE [Part::FeaturePython] Tube022  # WARN: FeaturePython — macro-defined, semantics opaque (R4)
  AttacherType = Attacher::AttachEngine3D
  Height = 12
  InnerRadius = 4.1
  OuterRadius = 9
  Placement = pos=(400,0,12) rot=(0,0,1;0rad)
FEATURE [Part::Cylinder] Cylinder190  label="Válec190"
  Angle = 360
  AttacherType = Attacher::AttachEngine3D
  Height = 100
  Placement = pos=(100,0,21) rot=(0.57735,0.57735,0.57735;2.0944rad)
  Radius = 1.5
FEATURE [Part::Cylinder] Cylinder191  label="Válec191"
  Angle = 360
  AttacherType = Attacher::AttachEngine3D
  Height = 100
  Placement = pos=(100,0,15) rot=(0.57735,0.57735,0.57735;2.0944rad)
  Radius = 1.5
FEATURE [Part::Box] Box014  label="Krychle014"
  AttacherType = Attacher::AttachEngine3D
  Height = 6
  Length = 6
  Placement = pos=(196.5,-3,18) rot=(0,0,1;1.5708rad)
  Width = 2
FEATURE [Part::Box] Box015  label="Krychle015"
  AttacherType = Attacher::AttachEngine3D
  Height = 6
  Length = 6
  Placement = pos=(196.5,-3,12) rot=(0,0,1;1.5708rad)
  Width = 2
FEATURE [Part::Wedge] Wedge030  label="Klín030"
  AttacherType = Attacher::AttachEngine3D
  Placement = pos=(400,0,12) rot=(0,0,1;0rad)
  X2max = 0
  X2min = 0
  Xmax = 10
  Xmin = -10
  Ymax = 0
  Ymin = -19
  Z2max = 12
  Z2min = 0
  Zmax = 12
  Zmin = 0
FEATURE [Part::Wedge] Wedge031  label="Klín031"
  AttacherType = Attacher::AttachEngine3D
  Placement = pos=(400,0,12) rot=(0,0,1;1.5708rad)
  X2max = 0
  X2min = 0
  Xmax = 10
  Xmin = -10
  Ymax = 0
  Ymin = -19
  Z2max = 12
  Z2min = 0
  Zmax = 12
  Zmin = 0
FEATURE [Part::Compound] Compound215
  Links = -> [Wedge028,Wedge030,Wedge031,Wedge029]
FEATURE [Part::Cut] Cut086
  Base = -> Tube022
  Tool = -> Compound215
FEATURE [Part::Compound] Compound216
  Links = -> [Cylinder190,Cylinder191]
  Placement = pos=(0,0,-20) rot=(0,0,1;0rad)
FEATURE [Part::Chamfer] Chamfer039
  Base = -> Cut086
  Edges = 2 edges r=0.8: [Edge17,Edge19]
FEATURE [Part::Chamfer] Chamfer040
  Base = -> Chamfer039
  Edges = 6 edges r=0.8: [Edge23,Edge28,Edge35,Edge40,Edge47,Edge49]
FEATURE [Part::Compound] Compound218
  Links = -> [Box014,Box015]
  Placement = pos=(0,0,-20) rot=(0,0,1;0rad)
FEATURE [Part::FeaturePython] Tube023  # WARN: FeaturePython — macro-defined, semantics opaque (R4)
  AttacherType = Attacher::AttachEngine3D
  Height = 58
  InnerRadius = 4.1
  OuterRadius = 9
  Placement = pos=(200,0,-8) rot=(0,0,1;0rad)
FEATURE [Part::Cut] Cut088
  Base = -> Tube023
  Tool = -> Compound218
FEATURE [Part::Cut] Cut087
  Base = -> Cut088
  Placement = pos=(200,0,-38) rot=(0,0,1;0rad)
  Tool = -> Compound216
FEATURE [Part::Cylinder] Cylinder192  label="Válec192"
  Angle = 360
  AttacherType = Attacher::AttachEngine3D
  Height = 12
  Placement = pos=(400,0,10) rot=(0,0,1;0rad)
  Radius = 4
FEATURE [Part::Chamfer] Chamfer038
  Base = -> Cylinder192
  Edges = 1 edges r=1: [Edge1]
FEATURE [Part::Compound] Compound217  label="J-max_motor-shaft-extended"
  Links = -> [Cut087,Chamfer038,Chamfer040]
FEATURE [Part::Cylinder] Cylinder194  label="Válec194"
  Angle = 360
  AttacherType = Attacher::AttachEngine3D
  Height = 2
  Placement = pos=(400,-7,25) rot=(0,0,1;0rad)
  Radius = 2
FEATURE [Part::Cylinder] Cylinder195  label="Válec195"
  Angle = 360
  AttacherType = Attacher::AttachEngine3D
  Height = 2
  Placement = pos=(395.05,-4.95,22) rot=(0,0,-1;0.785398rad)
  Radius = 2
FEATURE [Part::Cylinder] Cylinder196  label="Válec196"
  Angle = 360
  AttacherType = Attacher::AttachEngine3D
  Height = 20
  Placement = pos=(395.05,-4.95,4) rot=(0,0,-1;0.785398rad)
  Radius = 1
FEATURE [Part::Cylinder] Cylinder193  label="Válec193"
  Angle = 360
  AttacherType = Attacher::AttachEngine3D
  Height = 10
  Placement = pos=(400,-7,20) rot=(0,0,1;0rad)
  Radius = 1
FEATURE [Part::Cylinder] Cylinder197  label="Válec197"
  Angle = 360
  AttacherType = Attacher::AttachEngine3D
  Height = 2
  Placement = pos=(404.95,-4.95,22) rot=(0,0,1;0.785398rad)
  Radius = 2
FEATURE [Part::Cylinder] Cylinder198  label="Válec198"
  Angle = 360
  AttacherType = Attacher::AttachEngine3D
  Height = 2
  Placement = pos=(404.95,4.95,22) rot=(0,0,1;2.35619rad)
  Radius = 2
FEATURE [Part::Cylinder] Cylinder199  label="Válec199"
  Angle = 360
  AttacherType = Attacher::AttachEngine3D
  Height = 2
  Placement = pos=(395.05,4.95,22) rot=(0,0,1;3.92699rad)
  Radius = 2
FEATURE [Part::Compound] Compound219
  Links = -> [Cylinder195,Cylinder197,Cylinder198,Cylinder199]
FEATURE [Part::Cylinder] Cylinder200  label="Válec200"
  Angle = 360
  AttacherType = Attacher::AttachEngine3D
  Height = 20
  Placement = pos=(404.95,-4.95,4) rot=(0,0,1;0.785398rad)
  Radius = 1
FEATURE [Part::Cylinder] Cylinder201  label="Válec201"
  Angle = 360
  AttacherType = Attacher::AttachEngine3D
  Height = 20
  Placement = pos=(404.95,4.95,4) rot=(0,0,1;2.35619rad)
  Radius = 1
FEATURE [Part::Cylinder] Cylinder202  label="Válec202"
  Angle = 360
  AttacherType = Attacher::AttachEngine3D
  Height = 20
  Placement = pos=(395.05,4.95,4) rot=(0,0,1;3.92699rad)
  Radius = 1
FEATURE [Part::Compound] Compound220
  Links = -> [Cylinder196,Cylinder200,Cylinder201,Cylinder202]
FEATURE [Part::Cylinder] Cylinder203  label="Válec203"
  Angle = 360
  AttacherType = Attacher::AttachEngine3D
  Height = 2
  Placement = pos=(395.05,-4.95,22) rot=(0,0,-1;0.785398rad)
  Radius = 2
FEATURE [Part::Cylinder] Cylinder204  label="Válec204"
  Angle = 360
  AttacherType = Attacher::AttachEngine3D
  Height = 2
  Placement = pos=(395.05,4.95,22) rot=(0,0,1;3.92699rad)
  Radius = 2
FEATURE [Part::Cylinder] Cylinder205  label="Válec205"
  Angle = 360
  AttacherType = Attacher::AttachEngine3D
  Height = 2
  Placement = pos=(404.95,-4.95,22) rot=(0,0,1;0.785398rad)
  Radius = 2
FEATURE [Part::Cylinder] Cylinder206  label="Válec206"
  Angle = 360
  AttacherType = Attacher::AttachEngine3D
  Height = 2
  Placement = pos=(404.95,4.95,22) rot=(0,0,1;2.35619rad)
  Radius = 2
FEATURE [Part::Compound] Compound221
  Links = -> [Cylinder203,Cylinder205,Cylinder206,Cylinder204]
FEATURE [Part::Cylinder] Cylinder207  label="Válec207"
  Angle = 360
  AttacherType = Attacher::AttachEngine3D
  Height = 20
  Placement = pos=(404.95,4.95,4) rot=(0,0,1;2.35619rad)
  Radius = 1
FEATURE [Part::Cylinder] Cylinder208  label="Válec208"
  Angle = 360
  AttacherType = Attacher::AttachEngine3D
  Height = 20
  Placement = pos=(395.05,-4.95,4) rot=(0,0,-1;0.785398rad)
  Radius = 1
FEATURE [Part::Cylinder] Cylinder209  label="Válec209"
  Angle = 360
  AttacherType = Attacher::AttachEngine3D
  Height = 20
  Placement = pos=(404.95,-4.95,4) rot=(0,0,1;0.785398rad)
  Radius = 1
FEATURE [Part::Cylinder] Cylinder210  label="Válec210"
  Angle = 360
  AttacherType = Attacher::AttachEngine3D
  Height = 20
  Placement = pos=(395.05,4.95,4) rot=(0,0,1;3.92699rad)
  Radius = 1
FEATURE [Part::Compound] Compound222
  Links = -> [Cylinder208,Cylinder209,Cylinder207,Cylinder210]
FEATURE [Part::FeaturePython] Tube024  # WARN: FeaturePython — macro-defined, semantics opaque (R4)
  AttacherType = Attacher::AttachEngine3D
  Height = 66
  InnerRadius = 4.1
  OuterRadius = 9
  Placement = pos=(200,0,-8) rot=(0,0,1;0rad)
FEATURE [Part::Box] Box016  label="Krychle016"
  AttacherType = Attacher::AttachEngine3D
  Height = 6
  Length = 6
  Placement = pos=(196.5,-3,12) rot=(0,0,1;1.5708rad)
  Width = 2
FEATURE [Part::Cylinder] Cylinder211  label="Válec211"
  Angle = 360
  AttacherType = Attacher::AttachEngine3D
  Height = 100
  Placement = pos=(100,0,21) rot=(0.57735,0.57735,0.57735;2.0944rad)
  Radius = 1.5
FEATURE [Part::Box] Box017  label="Krychle017"
  AttacherType = Attacher::AttachEngine3D
  Height = 6
  Length = 6
  Placement = pos=(196.5,-3,18) rot=(0,0,1;1.5708rad)
  Width = 2
FEATURE [Part::Cylinder] Cylinder212  label="Válec212"
  Angle = 360
  AttacherType = Attacher::AttachEngine3D
  Height = 100
  Placement = pos=(100,0,15) rot=(0.57735,0.57735,0.57735;2.0944rad)
  Radius = 1.5
FEATURE [Part::Compound] Compound223
  Links = -> [Cylinder211,Cylinder212]
  Placement = pos=(0,0,-20) rot=(0,0,1;0rad)
FEATURE [Part::Compound] Compound224
  Links = -> [Box017,Box016]
  Placement = pos=(0,0,-20) rot=(0,0,1;0rad)
FEATURE [Part::Cut] Cut089
  Base = -> Tube024
  Tool = -> Compound224
FEATURE [Part::Cut] Cut090
  Base = -> Cut089
  Placement = pos=(200,0,-38) rot=(0,0,1;0rad)
  Tool = -> Compound223
FEATURE [Part::Cylinder] Cylinder213  label="Válec213"
  Angle = 360
  AttacherType = Attacher::AttachEngine3D
  Height = 12
  Placement = pos=(400,0,10) rot=(0,0,1;0rad)
  Radius = 4
FEATURE [Part::Chamfer] Chamfer041
  Base = -> Cylinder213
  Edges = 1 edges r=1: [Edge1]
FEATURE [Part::Wedge] Wedge032  label="Klín032"
  AttacherType = Attacher::AttachEngine3D
  Placement = pos=(400,0,12) rot=(0,0,1;1.5708rad)
  X2max = 0
  X2min = 0
  Xmax = 10
  Xmin = -10
  Ymax = 0
  Ymin = -19
  Z2max = 12
  Z2min = 0
  Zmax = 12
  Zmin = 0
FEATURE [Part::Wedge] Wedge033  label="Klín033"
  AttacherType = Attacher::AttachEngine3D
  Placement = pos=(400,0,12) rot=(0,0,-1;1.5708rad)
  X2max = 0
  X2min = 0
  Xmax = 10
  Xmin = -10
  Ymax = 0
  Ymin = -19
  Z2max = 12
  Z2min = 0
  Zmax = 12
  Zmin = 0
FEATURE [Part::Wedge] Wedge034  label="Klín034"
  AttacherType = Attacher::AttachEngine3D
  Placement = pos=(400,0,12) rot=(0,0,1;3.14159rad)
  X2max = 0
  X2min = 0
  Xmax = 10
  Xmin = -10
  Ymax = 0
  Ymin = -19
  Z2max = 12
  Z2min = 0
  Zmax = 12
  Zmin = 0
FEATURE [Part::Wedge] Wedge035  label="Klín035"
  AttacherType = Attacher::AttachEngine3D
  Placement = pos=(400,0,12) rot=(0,0,1;0rad)
  X2max = 0
  X2min = 0
  Xmax = 10
  Xmin = -10
  Ymax = 0
  Ymin = -19
  Z2max = 12
  Z2min = 0
  Zmax = 12
  Zmin = 0
FEATURE [Part::Compound] Compound225
  Links = -> [Wedge033,Wedge035,Wedge032,Wedge034]
FEATURE [Part::FeaturePython] Tube025  # WARN: FeaturePython — macro-defined, semantics opaque (R4)
  AttacherType = Attacher::AttachEngine3D
  Height = 12
  InnerRadius = 4.1
  OuterRadius = 9
  Placement = pos=(400,0,12) rot=(0,0,1;0rad)
FEATURE [Part::Cut] Cut091
  Base = -> Tube025
  Tool = -> Compound225
FEATURE [Part::Chamfer] Chamfer042
  Base = -> Cut091
  Edges = 2 edges r=0.8: [Edge17,Edge19]
FEATURE [Part::Chamfer] Chamfer043
  Base = -> Chamfer042
  Edges = 6 edges r=0.8: [Edge23,Edge28,Edge35,Edge40,Edge47,Edge49]
FEATURE [Part::Cut] Cut092
  Base = -> Cut090
  Placement = pos=(0,0,-8) rot=(0,0,1;0rad)
  Tool = -> Compound222
FEATURE [Part::Cut] Cut093
  Base = -> Chamfer043
  Tool = -> Compound220
FEATURE [Part::Cut] Cut094
  Base = -> Cut093
  Tool = -> Compound221
FEATURE [Part::Compound] Compound226  label="J-max_motor-shaft-extended-reinforced"
  Links = -> [Chamfer041,Cut092,Cut094]
FEATURE [Mesh::Feature] Mesh  label="J-max_motor-shaft-extended-reinforced (Meshed)"
